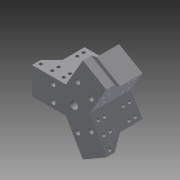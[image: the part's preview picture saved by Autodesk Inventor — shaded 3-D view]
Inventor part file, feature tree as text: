
AUTODESK INVENTOR PART (.ipt)
format: ipt  version: 2015 (Build 190159000, 159)  size: 220,160 bytes
history: native  units: mm
features: extrude x6, sketch x6, pattern_circular x3, projected_geometry x3
ambient origin geometry x8: Origin, YZ Plane, XZ Plane, XY Plane, X Axis, Y Axis, Z Axis, Center Point
bodies: Solid1 (feature_tree)
feature tree (18):
  extrude  "Extrusion1"  TaperAngle=60.0deg  [1 undecoded]
  extrude  "Extrusion2"  Depth=22.0mm
  pattern_circular  "Circular Pattern1"  Count=4  [1 undecoded]
  extrude  "Extrusion3"  Depth=40.0mm TaperAngle=0.0deg
  extrude  "Extrusion4"  Depth=30.0mm
  extrude  "Extrusion5"  Depth=30.0mm
  pattern_circular  "Circular Pattern2"  Count=10  [1 undecoded]
  extrude  "Extrusion6"  Depth=30.0mm
  pattern_circular  "Circular Pattern3"  [2 undecoded]
  sketch  "Sketch1"  dims[d0=26.0mm d1=60.0deg]
  sketch  "Sketch2"  dims[d2=22.0mm d3=22.0mm]
  projected_geometry  "Projected Loop1"
  sketch  "Sketch3"  dims[d4=22.0mm d5=40.0mm d6=0.0mm]
  sketch  "Sketch4"  dims[d7=45.0deg d9=40.0mm d10=0.0mm]
  projected_geometry  "Projected Loop2"
  sketch  "Sketch5"  dims[d11=30.0mm d12=360.0deg d14=8.0mm]
  projected_geometry  "Projected Loop3"
  sketch  "Sketch6"  dims[d15=18.5mm d17=8.0mm d18=100.0mm d19=0.0mm d20=3.0mm d21=3.0mm d22=3.0mm d23=3.0mm d24=3.0mm d25=3.0mm d26=3.0mm d27=3.0mm d28=3.0mm d29=5.0mm d30=5.0mm d31=6.0mm d32=6.0mm d33=11.0mm d34=7.0mm d35=4.0mm d36=100.0mm d37=0.0mm d38=5.0mm d39=5.0mm d40=5.5mm d41=5.5mm d42=9.5mm d43=100.0mm d44=0.0mm d45=30.0mm d46=360.0deg d48=12.8mm d49=12.8mm d50=30.0mm d51=0.0mm d52=30.0mm d53=360.0deg]
note: 5 required parameter values undecoded (feature->parameter linkage not recoverable at this tier; creation-order binding heuristic only, values carry confidence <= 0.55)
